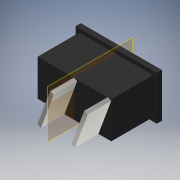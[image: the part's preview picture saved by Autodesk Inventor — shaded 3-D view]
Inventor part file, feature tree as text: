
AUTODESK INVENTOR PART (.ipt)
format: ipt  version: 2018 (Build 220112000, 112)  size: 166,912 bytes
history: native  units: mm
features: extrude x5, sketch x5, plane x1
ambient origin geometry x8: Origin, YZ Plane, XZ Plane, XY Plane, X Axis, Y Axis, Z Axis, Center Point
bodies: Solid1 (feature_tree), Solid2 (feature_tree), Solid3 (feature_tree)
feature tree (11):
  extrude  "Extrusion1"  Depth=14.1mm
  extrude  "Extrusion2"  Depth=1.5mm
  extrude  "Extrusion3"  Depth=1.5mm
  extrude  "Extrusion4"  Depth=9.1mm TaperAngle=0.0deg
  extrude  "Extrusion5"  Depth=31.5mm
  plane  "Work Plane1"
  sketch  "Sketch1"  dims[d0=28.6mm d1=14.1mm]
  sketch  "Sketch2"  dims[d2=16.2mm d3=0.0mm d5=1.5mm]
  sketch  "Sketch3"  dims[d6=12.217305mm d7=1.5mm]
  sketch  "Sketch4"  dims[d8=13.2mm d9=9.1mm d10=0.0mm]
  sketch  "Sketch5"  dims[d11=17.0mm d12=31.5mm d13=2.0mm d14=0.0mm d15=3.0mm d16=3.0mm d17=2.0mm d18=0.0mm d19=1.0mm d20=6.0mm d21=1.0mm d22=7.0mm d23=1.0mm d24=0.0mm]
